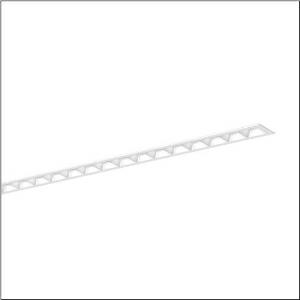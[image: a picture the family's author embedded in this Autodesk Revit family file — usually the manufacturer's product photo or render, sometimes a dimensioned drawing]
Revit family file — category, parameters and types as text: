
# Revit family: silica_21_51mx16db45wb
name_source: partatom
category: Lighting Fixtures
units: mm (PartAtom-declared; Revit-internal decimal feet)

## family parameters
Cut with Voids When Loaded = No
Host = Face
Light Source = No
Part Type = Normal
Room Calculation Point = No
Round Connector Dimension = Use Diameter
Shared = No

## types (1)
- --- (1 x LED, 5400 lm, 29.3 W, 4000K)
    Apparent Load = 29 VA
    CIE Flux Codes = 83 98 100 100 100
    Color Rendering = 80
    Color Temperature = 4000K
    Default Elevation = 1800 mm
    Description = Silica 21, office luminaire, primary light control with darklight reflector, of PMMA, white, CAT 2 (L<= 3000cd/m²), light emission: direct distribution, primary light characteristic: symmetric, installation type: recessed, LED, rated luminous flux: 5.400lm, luminous efficacy: 184lm/W, light colour: 840, colour temperature: 4000K, control gear: DALI 2, with terminal, 3+2-pole, max. 2.5mm², mains connection: 220..240V, AC, 50/60Hz, rated input power: 29.3W, luminaire housing, of aluminium, traffic white (RAL 9016), length: 1.528mm, width: 79mm, height: 53mm, protection rating (complete): IP20, insulation class (complete): insulation class I (protective earthing), certification: CE, ENEC, VDE, permissible operating ambient temperature: 0..+35°C, standard: EN 50419, packaging unit: 1 piece
    Height = 0 mm  [stored 0 ft]
    Lamp = 1 x LED
    Lamp Light Flux = 5400 lm
    Lamp Power = 29.3 W
    Lamp count = 1
    Length = 1527 mm
    Luminous efficacy = 184 lm/W
    Manufacturer = Siteco
    ModVariant = No
    Model = 51MX16DB45WB
    Mounting Place = Ceiling
    Mounting Type = Recessed
    Number of Poles = 1
    OnlyDefault = Yes
    Power Factor = 1
    Product Name = Silica 21
    Product group = office luminaire | ceiling recessed
    ProductGroupID = 400
    Protection Class = Protection class I
    Protection Degree = IP 20
    RLX_Detail_Level = 1
    RLX_Emergency_Light_Flux = 0 lm
    RLX_Emergency_Type = 0
    RLX_Emergency_Type_DB = No
    RlxData = <blob elided: 39525 chars, md5=5bc2987d>
    Socket = socket
    Standby Power = 0 W
    System Light Flux = 5400 lm
    System Power = 29 W
    Type Comments = factory setting: luminous flux: 100 % | dim-lin: 254 | 336 mA
    Type Image = l_1335884.jpg
    URL = http://relux.com
    VarID = @adj_124293
    Voltage = 0 V
    Weight = 0.00 kg
    Width = 79 mm

note: [stored X ft] marks values corroborated as IEEE doubles in the binary element streams (Revit-internal decimal feet)

## geometry (parser evidence)
native form markers: Blend x4, Sweep x11
no freeform markers — native parametric forms only
